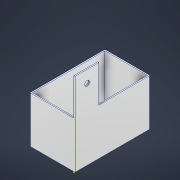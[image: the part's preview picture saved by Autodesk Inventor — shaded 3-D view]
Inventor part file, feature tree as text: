
AUTODESK INVENTOR PART (.ipt)
format: ipt  version: 2021 (Build 250183000, 183)  size: 198,656 bytes
history: native  units: mm
features: sketch x9, extrude x6, hole x2, fillet x2, chamfer x1, projected_geometry x1
ambient origin geometry x8: Origin, YZ Plane, XZ Plane, XY Plane, X Axis, Y Axis, Z Axis, Center Point
bodies: Solid1 (feature_tree)
feature tree (21):
  extrude  "base"  Depth=188.0mm
  extrude  "walls"  Depth=3.0mm
  extrude  "Extrusion8"  Depth=115.0mm
  hole  "Hole4"  [1 undecoded]
  fillet  "Fillet2"  Radius=54.0mm
  extrude  "Extrusion9"  TaperAngle=120.0deg  [1 undecoded]
  fillet  "Fillet3"  [1 undecoded]
  extrude  "Extrusion11"  Depth=1.0mm
  chamfer  "Chamfer4"  Distance=50.0mm
  sketch  "Sketch19"  dims[d103=6.0mm d104=8.0mm d105=4.0mm d106=2.0mm d107=90.0deg d108=8.0mm d109=20.594885mm d110=1.0mm]
  extrude  "Extrusion12"  Depth=6.0mm
  hole  "Hole6"  [1 undecoded]
  sketch  "Sketch1"  dims[d0=3.0mm d1=0.0mm d26=188.0mm]
  sketch  "Sketch7"  dims[d27=113.0mm d29=3.0mm]
  projected_geometry  "Projected Loop2"
  sketch  "Sketch13"  dims[d30=115.0mm d31=0.0mm d72=36.0mm d73=28.0mm]
  sketch  "Sketch14"  dims[d93=3.0mm d94=65.0mm d96=54.0mm d97=0.0mm]
  sketch  "Sketch15"  dims[d98=36.0mm d99=120.0deg d100=120.0deg]
  sketch  "Sketch17"  dims[d101=36.0mm]
  sketch  "Sketch20"  dims[d111=25.0mm d112=50.0mm d113=0.0mm]
  sketch  "Sketch21"  dims[d114=30.0mm d115=36.0mm d116=30.0mm d117=30.0mm d128=3.0mm d129=0.0mm d130=1.5mm d131=2.0mm d132=45.0deg d150=65.0mm d151=60.0mm d152=92.0mm d153=0.0mm d154=30.0mm d155=30.0mm d156=12.0mm d157=6.0mm d158=4.0mm d159=2.0mm d160=90.0deg d161=8.0mm d162=20.594885mm]
note: 4 required parameter values undecoded (feature->parameter linkage not recoverable at this tier; creation-order binding heuristic only, values carry confidence <= 0.55)
